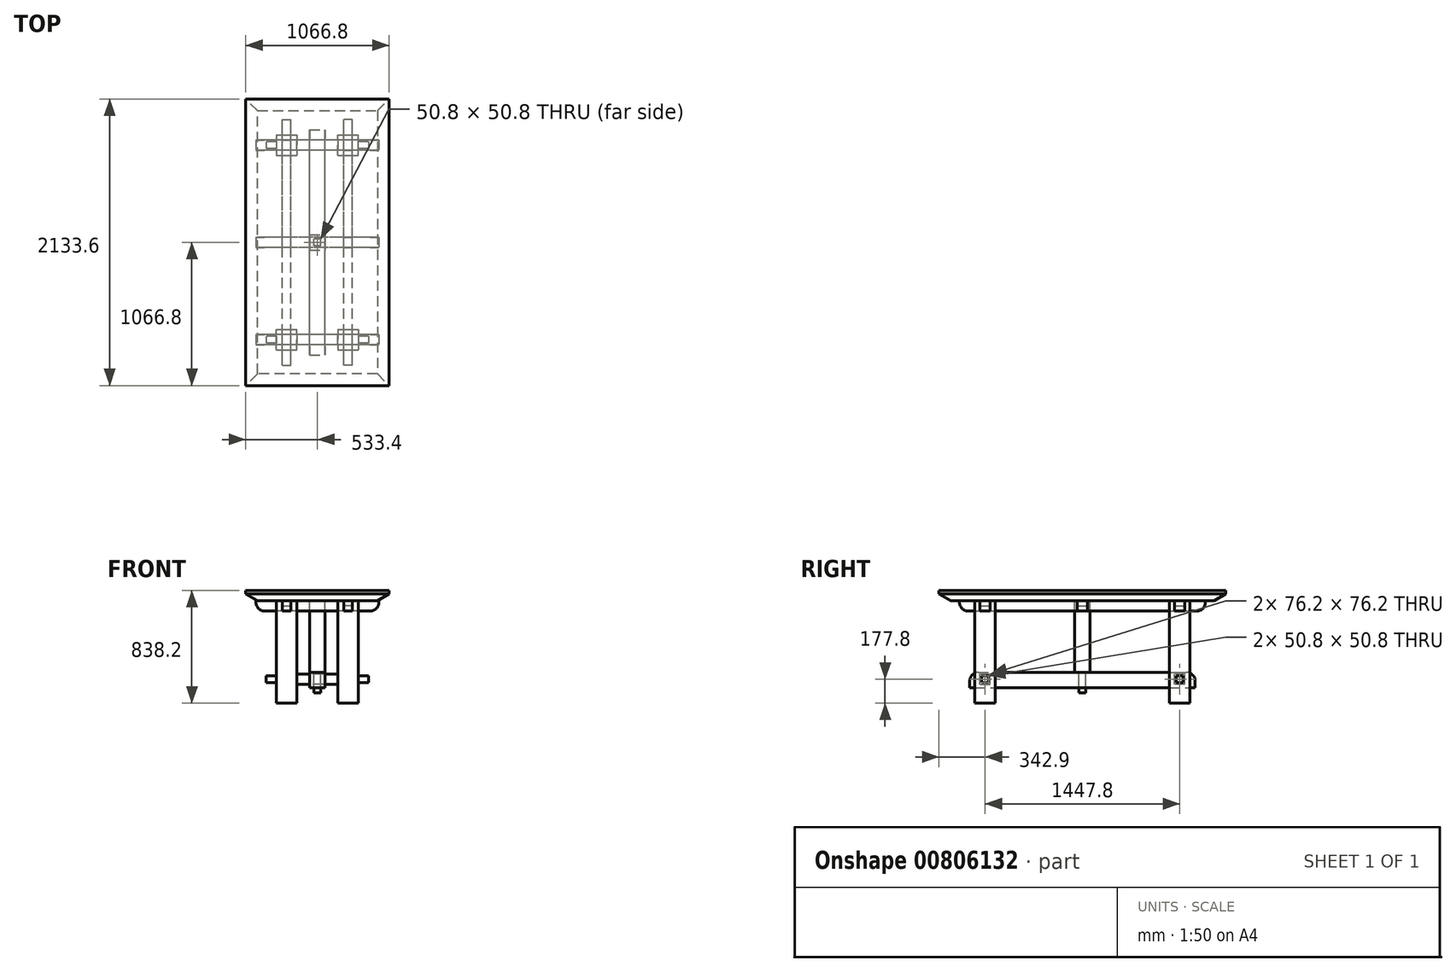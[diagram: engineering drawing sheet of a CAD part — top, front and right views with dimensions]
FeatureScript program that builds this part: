
annotation { "Feature Type Name" : "Feature", "Feature Type Description" : "" }
export const myFeature = defineFeature(function(context is Context, id is Id, definition is map)
    precondition{}
    {
        {
            var Q0;
            Q0=qCreatedBy(makeId("Top.planeOp"),FACE);
            var sketch = newSketch(context, id + "F0", { "sketchPlane" : qUnion([Q0])});
            skLineSegment(sketch, "E0.bottom", {"start": v(-533.4, -1066.8) * mm, "end": v(533.4, -1066.8) * mm});
            skLineSegment(sketch, "E0.top", {"start": v(-533.4, 1066.8) * mm, "end": v(533.4, 1066.8) * mm});
            skLineSegment(sketch, "E0.left", {"start": v(-533.4, -1066.8) * mm, "end": v(-533.4, 1066.8) * mm});
            skLineSegment(sketch, "E0.right", {"start": v(533.4, -1066.8) * mm, "end": v(533.4, 1066.8) * mm});
            skLineSegment(sketch, "E1", {"start": v(533.4, -1066.8) * mm, "end": v(-533.4, 1066.8) * mm, "construction": true});
            skSolve(sketch);
        }
        {
            var Q0;
            Q0 = qSketchRegion(id + "F0", true);
            extrude(context, id + "F1", {"entities" : qUnion([Q0]), "depth" : 76.2 * mm, "offsetDistance" : 25.4 * mm});
        }
        {
            var Q0;
            Q0=makeQuery(id+"F1.opExtrude","CAP_FACE",FACE,{"disambiguationData":[OSD([sQuery(id+"F0.wireOp",EDGE,"E0.bottom"),sQuery(id+"F0.wireOp",EDGE,"E0.top"),sQuery(id+"F0.wireOp",EDGE,"E0.left"),sQuery(id+"F0.wireOp",EDGE,"E0.right")])],"isStart":true});
            chamfer(context, id + "F2", {"entities" : qUnion([Q0]), "chamferType" : ChamferType.OFFSET_ANGLE, "width" : 50.8 * mm, "oppositeDirection" : false, "angle" : 60 * degree, "tangentPropagation" : true});
        }
        {
            var Q0;
            Q0=qCreatedBy(makeId("Right.planeOp"),FACE);
            var sketch = newSketch(context, id + "F3", { "sketchPlane" : qUnion([Q0])});
            skLineSegment(sketch, "E2.bottom", {"start": v(762, -76.2) * mm, "end": v(685.8, -76.2) * mm});
            skLineSegment(sketch, "E2.top", {"start": v(762, 0) * mm, "end": v(685.8, 0) * mm});
            skLineSegment(sketch, "E2.left", {"start": v(762, -76.2) * mm, "end": v(762, 0) * mm});
            skLineSegment(sketch, "E2.right", {"start": v(685.8, -76.2) * mm, "end": v(685.8, 0) * mm});
            skLineSegment(sketch, "E3.bottom", {"start": v(38.1, -76.2) * mm, "end": v(-38.1, -76.2) * mm});
            skLineSegment(sketch, "E3.top", {"start": v(38.1, 0) * mm, "end": v(-38.1, 0) * mm});
            skLineSegment(sketch, "E3.left", {"start": v(38.1, -76.2) * mm, "end": v(38.1, 0) * mm});
            skLineSegment(sketch, "E3.right", {"start": v(-38.1, -76.2) * mm, "end": v(-38.1, 0) * mm});
            skLineSegment(sketch, "E4.bottom", {"start": v(-685.8, -76.2) * mm, "end": v(-762, -76.2) * mm});
            skLineSegment(sketch, "E4.top", {"start": v(-685.8, 0) * mm, "end": v(-762, 0) * mm});
            skLineSegment(sketch, "E4.left", {"start": v(-685.8, -76.2) * mm, "end": v(-685.8, 0) * mm});
            skLineSegment(sketch, "E4.right", {"start": v(-762, -76.2) * mm, "end": v(-762, 0) * mm});
            skLineSegment(sketch, "E5", {"start": v(685.8, -76.2) * mm, "end": v(38.1, -76.2) * mm, "construction": true});
            skLineSegment(sketch, "E6", {"start": v(-38.1, -76.2) * mm, "end": v(-685.8, -76.2) * mm, "construction": true});
            skSolve(sketch);
        }
        {
            var Q0;
            Q0 = qSketchRegion(id + "F3", true);
            extrude(context, id + "F4", {"entities" : qUnion([Q0]), "endBound" : BoundingType.SYMMETRIC, "depth" : 914.4 * mm, "offsetDistance" : 25.4 * mm});
        }
        {
            var Q0;
            Q0=makeQuery(id+"F4.opExtrude","SWEPT_FACE",FACE,{"disambiguationData":[OSD([sQuery(id+"F3.wireOp",EDGE,"E2.left")])]});
            var sketch = newSketch(context, id + "F5", { "sketchPlane" : qUnion([Q0])});
            skLineSegment(sketch, "E7.bottom", {"start": v(-260.35, 0) * mm, "end": v(-196.85, 0) * mm});
            skLineSegment(sketch, "E7.top", {"start": v(-260.35, -38.1) * mm, "end": v(-196.85, -38.1) * mm});
            skLineSegment(sketch, "E7.left", {"start": v(-260.35, 0) * mm, "end": v(-260.35, -38.1) * mm});
            skLineSegment(sketch, "E7.right", {"start": v(-196.85, 0) * mm, "end": v(-196.85, -38.1) * mm});
            skLineSegment(sketch, "E8.bottom", {"start": v(260.35, 0) * mm, "end": v(196.85, 0) * mm});
            skLineSegment(sketch, "E8.top", {"start": v(260.35, -38.1) * mm, "end": v(196.85, -38.1) * mm});
            skLineSegment(sketch, "E8.left", {"start": v(196.85, 0) * mm, "end": v(196.85, -38.1) * mm});
            skLineSegment(sketch, "E8.right", {"start": v(260.35, 0) * mm, "end": v(260.35, -38.1) * mm});
            skLineSegment(sketch, "E9", {"start": v(-228.6, -38.1) * mm, "end": v(-228.6, -76.2) * mm, "construction": true});
            skLineSegment(sketch, "E10", {"start": v(228.6, -38.1) * mm, "end": v(228.6, -76.2) * mm, "construction": true});
            skLineSegment(sketch, "E11", {"start": v(-457.2, -38.1) * mm, "end": v(-260.35, -38.1) * mm, "construction": true});
            skLineSegment(sketch, "E12", {"start": v(260.35, -38.1) * mm, "end": v(457.2, -38.1) * mm, "construction": true});
            skSolve(sketch);
        }
        {
            var Q0;
            Q0 = qSketchRegion(id + "F5", true);
            extrude(context, id + "F6", {"entities" : qUnion([Q0]), "operationType" : NewBodyOperationType.REMOVE, "endBound" : BoundingType.THROUGH_ALL, "oppositeDirection" : true, "depth" : 25.4 * mm, "offsetDistance" : 25.4 * mm});
        }
        {
            var Q0;
            Q0=qCreatedBy(makeId("Front.planeOp"),FACE);
            var sketch = newSketch(context, id + "F7", { "sketchPlane" : qUnion([Q0])});
            skLineSegment(sketch, "E13.bottom", {"start": v(260.35, 0) * mm, "end": v(196.85, 0) * mm});
            skLineSegment(sketch, "E13.top", {"start": v(260.35, -76.2) * mm, "end": v(196.85, -76.2) * mm});
            skLineSegment(sketch, "E13.left", {"start": v(260.35, 0) * mm, "end": v(260.35, -76.2) * mm});
            skLineSegment(sketch, "E13.right", {"start": v(196.85, 0) * mm, "end": v(196.85, -76.2) * mm});
            skLineSegment(sketch, "E14.bottom", {"start": v(-260.35, 0) * mm, "end": v(-196.85, 0) * mm});
            skLineSegment(sketch, "E14.top", {"start": v(-260.35, -76.2) * mm, "end": v(-196.85, -76.2) * mm});
            skLineSegment(sketch, "E14.left", {"start": v(-260.35, 0) * mm, "end": v(-260.35, -76.2) * mm});
            skLineSegment(sketch, "E14.right", {"start": v(-196.85, 0) * mm, "end": v(-196.85, -76.2) * mm});
            skSolve(sketch);
        }
        {
            var Q0;
            Q0 = qSketchRegion(id + "F7", true);
            extrude(context, id + "F8", {"entities" : qUnion([Q0]), "endBound" : BoundingType.SYMMETRIC, "depth" : 1828.8 * mm, "offsetDistance" : 25.4 * mm});
        }
        {
            var Q0;
            Q0=makeQuery(id+"F4.opExtrude","SWEPT_BODY",BODY,{"disambiguationData":[OSD([sQuery(id+"F3.wireOp",EDGE,"E2.bottom"),sQuery(id+"F3.wireOp",EDGE,"E2.top"),sQuery(id+"F3.wireOp",EDGE,"E2.left"),sQuery(id+"F3.wireOp",EDGE,"E2.right")])]});
            var Q1;
            Q1=makeQuery(id+"F4.opExtrude","SWEPT_BODY",BODY,{"disambiguationData":[OSD([sQuery(id+"F3.wireOp",EDGE,"E3.bottom"),sQuery(id+"F3.wireOp",EDGE,"E3.top"),sQuery(id+"F3.wireOp",EDGE,"E3.left"),sQuery(id+"F3.wireOp",EDGE,"E3.right")])]});
            var Q2;
            Q2=makeQuery(id+"F4.opExtrude","SWEPT_BODY",BODY,{"disambiguationData":[OSD([sQuery(id+"F3.wireOp",EDGE,"E4.bottom"),sQuery(id+"F3.wireOp",EDGE,"E4.top"),sQuery(id+"F3.wireOp",EDGE,"E4.left"),sQuery(id+"F3.wireOp",EDGE,"E4.right")])]});
            var Q3;
            Q3=makeQuery(id+"F8.opExtrude","SWEPT_BODY",BODY,{"disambiguationData":[OSD([sQuery(id+"F7.wireOp",EDGE,"E13.bottom"),sQuery(id+"F7.wireOp",EDGE,"E13.top"),sQuery(id+"F7.wireOp",EDGE,"E13.left"),sQuery(id+"F7.wireOp",EDGE,"E13.right")])]});
            var Q4;
            Q4=makeQuery(id+"F8.opExtrude","SWEPT_BODY",BODY,{"disambiguationData":[OSD([sQuery(id+"F7.wireOp",EDGE,"E14.bottom"),sQuery(id+"F7.wireOp",EDGE,"E14.top"),sQuery(id+"F7.wireOp",EDGE,"E14.left"),sQuery(id+"F7.wireOp",EDGE,"E14.right")])]});
            booleanBodies(context, id + "F9", {"operationType" : BooleanOperationType.SUBTRACTION, "tools" : qUnion([Q0, Q1, Q2]), "targets" : qUnion([Q3, Q4]), "keepTools" : true});
        }
        {
            var Q0;
            Q0=makeQuery(id+"F1.opExtrude","CAP_FACE",FACE,{"disambiguationData":[OSD([sQuery(id+"F0.wireOp",EDGE,"E0.bottom"),sQuery(id+"F0.wireOp",EDGE,"E0.top"),sQuery(id+"F0.wireOp",EDGE,"E0.left"),sQuery(id+"F0.wireOp",EDGE,"E0.right")])],"isStart":true});
            var sketch = newSketch(context, id + "F10", { "sketchPlane" : qUnion([Q0])});
            skLineSegment(sketch, "E15.bottom", {"start": v(-57.15, -57.15) * mm, "end": v(57.15, -57.15) * mm});
            skLineSegment(sketch, "E15.top", {"start": v(-57.15, 57.15) * mm, "end": v(57.15, 57.15) * mm});
            skLineSegment(sketch, "E15.left", {"start": v(-57.15, -57.15) * mm, "end": v(-57.15, 57.15) * mm});
            skLineSegment(sketch, "E15.right", {"start": v(57.15, -57.15) * mm, "end": v(57.15, 57.15) * mm});
            skLineSegment(sketch, "E16", {"start": v(-57.15, 57.15) * mm, "end": v(57.15, -57.15) * mm, "construction": true});
            skSolve(sketch);
        }
        {
            var Q0;
            Q0 = qSketchRegion(id + "F10", true);
            extrude(context, id + "F11", {"entities" : qUnion([Q0]), "depth" : 533.4 * mm, "offsetDistance" : 25.4 * mm});
        }
        {
            var Q0;
            Q0=makeQuery(id+"F4.opExtrude","SWEPT_BODY",BODY,{"disambiguationData":[OSD([sQuery(id+"F3.wireOp",EDGE,"E3.bottom"),sQuery(id+"F3.wireOp",EDGE,"E3.top"),sQuery(id+"F3.wireOp",EDGE,"E3.left"),sQuery(id+"F3.wireOp",EDGE,"E3.right")])]});
            var Q1;
            Q1=makeQuery(id+"F11.opExtrude","SWEPT_BODY",BODY,{"disambiguationData":[OSD([sQuery(id+"F10.wireOp",EDGE,"E15.bottom"),sQuery(id+"F10.wireOp",EDGE,"E15.top"),sQuery(id+"F10.wireOp",EDGE,"E15.left"),sQuery(id+"F10.wireOp",EDGE,"E15.right")])]});
            booleanBodies(context, id + "F12", {"operationType" : BooleanOperationType.SUBTRACTION, "tools" : qUnion([Q0]), "targets" : qUnion([Q1]), "keepTools" : true});
        }
        {
            var Q0;
            Q0=makeQuery(id+"F1.opExtrude","CAP_FACE",FACE,{"disambiguationData":[OSD([sQuery(id+"F0.wireOp",EDGE,"E0.bottom"),sQuery(id+"F0.wireOp",EDGE,"E0.top"),sQuery(id+"F0.wireOp",EDGE,"E0.left"),sQuery(id+"F0.wireOp",EDGE,"E0.right")])],"isStart":true});
            var sketch = newSketch(context, id + "F13", { "sketchPlane" : qUnion([Q0])});
            skLineSegment(sketch, "E17.bottom", {"start": v(152.4, 647.7) * mm, "end": v(304.8, 647.7) * mm});
            skLineSegment(sketch, "E17.top", {"start": v(152.4, 800.1) * mm, "end": v(304.8, 800.1) * mm});
            skLineSegment(sketch, "E17.left", {"start": v(152.4, 647.7) * mm, "end": v(152.4, 800.1) * mm});
            skLineSegment(sketch, "E17.right", {"start": v(304.8, 647.7) * mm, "end": v(304.8, 800.1) * mm});
            skLineSegment(sketch, "E18.bottom", {"start": v(152.4, -647.7) * mm, "end": v(304.8, -647.7) * mm});
            skLineSegment(sketch, "E18.top", {"start": v(152.4, -800.1) * mm, "end": v(304.8, -800.1) * mm});
            skLineSegment(sketch, "E18.left", {"start": v(152.4, -647.7) * mm, "end": v(152.4, -800.1) * mm});
            skLineSegment(sketch, "E18.right", {"start": v(304.8, -647.7) * mm, "end": v(304.8, -800.1) * mm});
            skLineSegment(sketch, "E19.bottom", {"start": v(-304.8, -800.1) * mm, "end": v(-152.4, -800.1) * mm});
            skLineSegment(sketch, "E19.top", {"start": v(-304.8, -647.7) * mm, "end": v(-152.4, -647.7) * mm});
            skLineSegment(sketch, "E19.left", {"start": v(-304.8, -800.1) * mm, "end": v(-304.8, -647.7) * mm});
            skLineSegment(sketch, "E19.right", {"start": v(-152.4, -800.1) * mm, "end": v(-152.4, -647.7) * mm});
            skLineSegment(sketch, "E20.bottom", {"start": v(-304.8, 800.1) * mm, "end": v(-152.4, 800.1) * mm});
            skLineSegment(sketch, "E20.top", {"start": v(-304.8, 647.7) * mm, "end": v(-152.4, 647.7) * mm});
            skLineSegment(sketch, "E20.left", {"start": v(-304.8, 800.1) * mm, "end": v(-304.8, 647.7) * mm});
            skLineSegment(sketch, "E20.right", {"start": v(-152.4, 800.1) * mm, "end": v(-152.4, 647.7) * mm});
            skLineSegment(sketch, "E21", {"start": v(-144.46, 565.34) * mm, "end": v(-140.26, 569.66) * mm, "construction": true});
            skLineSegment(sketch, "E22", {"start": v(-152.4, 647.7) * mm, "end": v(-304.8, 800.1) * mm, "construction": true});
            skLineSegment(sketch, "E23", {"start": v(-196.85, 762) * mm, "end": v(-228.6, 723.9) * mm, "construction": true});
            skLineSegment(sketch, "E24", {"start": v(-228.6, 723.9) * mm, "end": v(-260.35, 685.8) * mm, "construction": true});
            skLineSegment(sketch, "E25", {"start": v(260.35, -685.8) * mm, "end": v(228.6, -723.9) * mm, "construction": true});
            skLineSegment(sketch, "E26", {"start": v(228.6, -723.9) * mm, "end": v(196.85, -762) * mm, "construction": true});
            skLineSegment(sketch, "E27", {"start": v(152.4, -647.7) * mm, "end": v(304.8, -800.1) * mm, "construction": true});
            skSolve(sketch);
        }
        {
            var Q0;
            Q0 = qSketchRegion(id + "F13", true);
            extrude(context, id + "F14", {"entities" : qUnion([Q0]), "depth" : 762 * mm, "offsetDistance" : 25.4 * mm});
        }
        {
            var Q0;
            Q0=makeQuery(id+"F4.opExtrude","SWEPT_BODY",BODY,{"disambiguationData":[OSD([sQuery(id+"F3.wireOp",EDGE,"E4.bottom"),sQuery(id+"F3.wireOp",EDGE,"E4.top"),sQuery(id+"F3.wireOp",EDGE,"E4.left"),sQuery(id+"F3.wireOp",EDGE,"E4.right")])]});
            var Q1;
            Q1=makeQuery(id+"F8.opExtrude","SWEPT_BODY",BODY,{"disambiguationData":[OSD([sQuery(id+"F7.wireOp",EDGE,"E14.bottom"),sQuery(id+"F7.wireOp",EDGE,"E14.top"),sQuery(id+"F7.wireOp",EDGE,"E14.left"),sQuery(id+"F7.wireOp",EDGE,"E14.right")])]});
            var Q2;
            Q2=makeQuery(id+"F8.opExtrude","SWEPT_BODY",BODY,{"disambiguationData":[OSD([sQuery(id+"F7.wireOp",EDGE,"E13.bottom"),sQuery(id+"F7.wireOp",EDGE,"E13.top"),sQuery(id+"F7.wireOp",EDGE,"E13.left"),sQuery(id+"F7.wireOp",EDGE,"E13.right")])]});
            var Q3;
            Q3=makeQuery(id+"F4.opExtrude","SWEPT_BODY",BODY,{"disambiguationData":[OSD([sQuery(id+"F3.wireOp",EDGE,"E3.bottom"),sQuery(id+"F3.wireOp",EDGE,"E3.top"),sQuery(id+"F3.wireOp",EDGE,"E3.left"),sQuery(id+"F3.wireOp",EDGE,"E3.right")])]});
            var Q4;
            Q4=makeQuery(id+"F4.opExtrude","SWEPT_BODY",BODY,{"disambiguationData":[OSD([sQuery(id+"F3.wireOp",EDGE,"E2.bottom"),sQuery(id+"F3.wireOp",EDGE,"E2.top"),sQuery(id+"F3.wireOp",EDGE,"E2.left"),sQuery(id+"F3.wireOp",EDGE,"E2.right")])]});
            var Q5;
            Q5=makeQuery(id+"F14.opExtrude","SWEPT_BODY",BODY,{"disambiguationData":[OSD([sQuery(id+"F13.wireOp",EDGE,"E17.bottom"),sQuery(id+"F13.wireOp",EDGE,"E17.top"),sQuery(id+"F13.wireOp",EDGE,"E17.left"),sQuery(id+"F13.wireOp",EDGE,"E17.right")])]});
            var Q6;
            Q6=makeQuery(id+"F14.opExtrude","SWEPT_BODY",BODY,{"disambiguationData":[OSD([sQuery(id+"F13.wireOp",EDGE,"E20.bottom"),sQuery(id+"F13.wireOp",EDGE,"E20.top"),sQuery(id+"F13.wireOp",EDGE,"E20.left"),sQuery(id+"F13.wireOp",EDGE,"E20.right")])]});
            var Q7;
            Q7=makeQuery(id+"F14.opExtrude","SWEPT_BODY",BODY,{"disambiguationData":[OSD([sQuery(id+"F13.wireOp",EDGE,"E19.bottom"),sQuery(id+"F13.wireOp",EDGE,"E19.top"),sQuery(id+"F13.wireOp",EDGE,"E19.left"),sQuery(id+"F13.wireOp",EDGE,"E19.right")])]});
            var Q8;
            Q8=makeQuery(id+"F14.opExtrude","SWEPT_BODY",BODY,{"disambiguationData":[OSD([sQuery(id+"F13.wireOp",EDGE,"E18.bottom"),sQuery(id+"F13.wireOp",EDGE,"E18.top"),sQuery(id+"F13.wireOp",EDGE,"E18.left"),sQuery(id+"F13.wireOp",EDGE,"E18.right")])]});
            booleanBodies(context, id + "F15", {"operationType" : BooleanOperationType.SUBTRACTION, "tools" : qUnion([Q0, Q1, Q2, Q3, Q4]), "targets" : qUnion([Q5, Q6, Q7, Q8]), "keepTools" : true});
        }
        {
            var Q0;
            Q0=makeQuery(id+"F11.opExtrude","CAP_FACE",FACE,{"disambiguationData":[OSD([sQuery(id+"F10.wireOp",EDGE,"E15.bottom"),sQuery(id+"F10.wireOp",EDGE,"E15.top"),sQuery(id+"F10.wireOp",EDGE,"E15.left"),sQuery(id+"F10.wireOp",EDGE,"E15.right")])],"isStart":false});
            var sketch = newSketch(context, id + "F16", { "sketchPlane" : qUnion([Q0])});
            skLineSegment(sketch, "E28.bottom", {"start": v(25.4, 25.4) * mm, "end": v(-25.4, 25.4) * mm});
            skLineSegment(sketch, "E28.top", {"start": v(25.4, -25.4) * mm, "end": v(-25.4, -25.4) * mm});
            skLineSegment(sketch, "E28.left", {"start": v(25.4, 25.4) * mm, "end": v(25.4, -25.4) * mm});
            skLineSegment(sketch, "E28.right", {"start": v(-25.4, 25.4) * mm, "end": v(-25.4, -25.4) * mm});
            skLineSegment(sketch, "E29", {"start": v(0, -57.15) * mm, "end": v(0, -25.4) * mm, "construction": true});
            skLineSegment(sketch, "E30", {"start": v(-25.4, 0) * mm, "end": v(-57.15, 0) * mm, "construction": true});
            skLineSegment(sketch, "E31", {"start": v(0, 25.4) * mm, "end": v(0, 57.15) * mm, "construction": true});
            skLineSegment(sketch, "E32", {"start": v(25.4, 0) * mm, "end": v(57.15, 0) * mm, "construction": true});
            skSolve(sketch);
        }
        {
            var Q0;
            Q0 = qSketchRegion(id + "F16", true);
            extrude(context, id + "F17", {"entities" : qUnion([Q0]), "operationType" : NewBodyOperationType.ADD, "depth" : 152.4 * mm, "offsetDistance" : 25.4 * mm});
        }
        {
            var Q0;
            Q0=makeQuery(id+"F14.opExtrude","SWEPT_FACE",FACE,{"disambiguationData":[OSD([sQuery(id+"F13.wireOp",EDGE,"E19.left")])]});
            var sketch = newSketch(context, id + "F18", { "sketchPlane" : qUnion([Q0])});
            skLineSegment(sketch, "E33.bottom", {"start": v(-749.3, -609.6) * mm, "end": v(-698.5, -609.6) * mm});
            skLineSegment(sketch, "E33.top", {"start": v(-749.3, -558.8) * mm, "end": v(-698.5, -558.8) * mm});
            skLineSegment(sketch, "E33.left", {"start": v(-749.3, -609.6) * mm, "end": v(-749.3, -558.8) * mm});
            skLineSegment(sketch, "E33.right", {"start": v(-698.5, -609.6) * mm, "end": v(-698.5, -558.8) * mm});
            skLineSegment(sketch, "E34.bottom", {"start": v(698.5, -609.6) * mm, "end": v(749.3, -609.6) * mm});
            skLineSegment(sketch, "E34.top", {"start": v(698.5, -558.8) * mm, "end": v(749.3, -558.8) * mm});
            skLineSegment(sketch, "E34.left", {"start": v(698.5, -609.6) * mm, "end": v(698.5, -558.8) * mm});
            skLineSegment(sketch, "E34.right", {"start": v(749.3, -609.6) * mm, "end": v(749.3, -558.8) * mm});
            skLineSegment(sketch, "E35", {"start": v(749.3, -584.2) * mm, "end": v(800.1, -584.2) * mm, "construction": true});
            skLineSegment(sketch, "E36", {"start": v(698.5, -584.2) * mm, "end": v(647.7, -584.2) * mm, "construction": true});
            skLineSegment(sketch, "E37", {"start": v(-698.5, -584.2) * mm, "end": v(-647.7, -584.2) * mm, "construction": true});
            skPoint(sketch, "E37.endSnap0", {"position": v(-698.5, -584.2) * mm});
            skLineSegment(sketch, "E38", {"start": v(-749.3, -584.2) * mm, "end": v(-800.1, -584.2) * mm, "construction": true});
            skSolve(sketch);
        }
        {
            var Q0;
            Q0 = qSketchRegion(id + "F18", true);
            extrude(context, id + "F19", {"entities" : qUnion([Q0]), "operationType" : NewBodyOperationType.REMOVE, "endBound" : BoundingType.THROUGH_ALL, "oppositeDirection" : true, "depth" : 25.4 * mm, "offsetDistance" : 25.4 * mm});
        }
        {
            var Q0;
            Q0=qCreatedBy(makeId("Right.planeOp"),FACE);
            var sketch = newSketch(context, id + "F20", { "sketchPlane" : qUnion([Q0])});
            skLineSegment(sketch, "E39.bottom", {"start": v(749.3, -609.6) * mm, "end": v(698.5, -609.6) * mm});
            skLineSegment(sketch, "E39.top", {"start": v(749.3, -558.8) * mm, "end": v(698.5, -558.8) * mm});
            skLineSegment(sketch, "E39.left", {"start": v(749.3, -609.6) * mm, "end": v(749.3, -558.8) * mm});
            skLineSegment(sketch, "E39.right", {"start": v(698.5, -609.6) * mm, "end": v(698.5, -558.8) * mm});
            skLineSegment(sketch, "E40.bottom", {"start": v(-698.5, -609.6) * mm, "end": v(-749.3, -609.6) * mm});
            skLineSegment(sketch, "E40.top", {"start": v(-698.5, -558.8) * mm, "end": v(-749.3, -558.8) * mm});
            skLineSegment(sketch, "E40.left", {"start": v(-698.5, -609.6) * mm, "end": v(-698.5, -558.8) * mm});
            skLineSegment(sketch, "E40.right", {"start": v(-749.3, -609.6) * mm, "end": v(-749.3, -558.8) * mm});
            skSolve(sketch);
        }
        {
            var Q0;
            Q0 = qSketchRegion(id + "F20", true);
            extrude(context, id + "F21", {"entities" : qUnion([Q0]), "endBound" : BoundingType.SYMMETRIC, "depth" : 762 * mm, "offsetDistance" : 25.4 * mm});
        }
        {
            var Q0;
            Q0=qCreatedBy(makeId("Right.planeOp"),FACE);
            var sketch = newSketch(context, id + "F22", { "sketchPlane" : qUnion([Q0])});
            skLineSegment(sketch, "E41.bottom", {"start": v(-685.8, -546.1) * mm, "end": v(-762, -546.1) * mm});
            skLineSegment(sketch, "E41.top", {"start": v(-685.8, -622.3) * mm, "end": v(-762, -622.3) * mm});
            skLineSegment(sketch, "E41.left", {"start": v(-685.8, -546.1) * mm, "end": v(-685.8, -622.3) * mm});
            skLineSegment(sketch, "E41.right", {"start": v(-762, -546.1) * mm, "end": v(-762, -622.3) * mm});
            skLineSegment(sketch, "E42.bottom", {"start": v(685.8, -546.1) * mm, "end": v(762, -546.1) * mm});
            skLineSegment(sketch, "E42.top", {"start": v(685.8, -622.3) * mm, "end": v(762, -622.3) * mm});
            skLineSegment(sketch, "E42.left", {"start": v(685.8, -546.1) * mm, "end": v(685.8, -622.3) * mm});
            skLineSegment(sketch, "E42.right", {"start": v(762, -546.1) * mm, "end": v(762, -622.3) * mm});
            skLineSegment(sketch, "E43", {"start": v(723.9, -546.1) * mm, "end": v(723.9, -558.8) * mm, "construction": true});
            skLineSegment(sketch, "E44", {"start": v(685.8, -584.2) * mm, "end": v(698.5, -584.2) * mm, "construction": true});
            skLineSegment(sketch, "E45", {"start": v(723.9, -622.3) * mm, "end": v(723.9, -609.6) * mm, "construction": true});
            skPoint(sketch, "E45.endSnap0", {"position": v(723.9, -622.3) * mm});
            skLineSegment(sketch, "E46", {"start": v(762, -584.2) * mm, "end": v(749.3, -584.2) * mm, "construction": true});
            skLineSegment(sketch, "E47", {"start": v(-723.9, -546.1) * mm, "end": v(-723.9, -558.8) * mm, "construction": true});
            skLineSegment(sketch, "E48", {"start": v(-723.9, -622.3) * mm, "end": v(-723.9, -609.6) * mm, "construction": true});
            skLineSegment(sketch, "E49", {"start": v(-762, -584.2) * mm, "end": v(-749.3, -584.2) * mm, "construction": true});
            skLineSegment(sketch, "E50", {"start": v(-685.8, -584.2) * mm, "end": v(-698.5, -584.2) * mm, "construction": true});
            skSolve(sketch);
        }
        {
            var Q0;
            Q0 = qSketchRegion(id + "F22", true);
            var Q1;
            Q1=makeQuery(id+"F14.opExtrude","SWEPT_FACE",FACE,{"disambiguationData":[OSD([sQuery(id+"F13.wireOp",EDGE,"E17.left")])]});
            var Q2;
            Q2=makeQuery(id+"F14.opExtrude","SWEPT_FACE",FACE,{"disambiguationData":[OSD([sQuery(id+"F13.wireOp",EDGE,"E20.right")])]});
            extrude(context, id + "F23", {"entities" : qUnion([Q0]), "operationType" : NewBodyOperationType.ADD, "endBound" : BoundingType.UP_TO_SURFACE, "depth" : 25.4 * mm, "endBoundEntityFace" : qUnion([Q1]), "offsetDistance" : 25.4 * mm, "hasSecondDirection" : true, "secondDirectionBound" : SecondDirectionBoundingType.UP_TO_SURFACE, "secondDirectionOppositeDirection" : true, "secondDirectionDepth" : 25.4 * mm, "secondDirectionBoundEntityFace" : qUnion([Q2])});
        }
        {
            var Q0;
            Q0=qCreatedBy(makeId("Front.planeOp"),FACE);
            var sketch = newSketch(context, id + "F24", { "sketchPlane" : qUnion([Q0])});
            skLineSegment(sketch, "E51.bottom", {"start": v(-57.15, -533.4) * mm, "end": v(57.15, -533.4) * mm});
            skLineSegment(sketch, "E51.top", {"start": v(-57.15, -647.7) * mm, "end": v(57.15, -647.7) * mm});
            skLineSegment(sketch, "E51.left", {"start": v(-57.15, -533.4) * mm, "end": v(-57.15, -647.7) * mm});
            skLineSegment(sketch, "E51.right", {"start": v(57.15, -533.4) * mm, "end": v(57.15, -647.7) * mm});
            skSolve(sketch);
        }
        {
            var Q0;
            Q0 = qSketchRegion(id + "F24", true);
            extrude(context, id + "F25", {"entities" : qUnion([Q0]), "endBound" : BoundingType.SYMMETRIC, "depth" : 1676.4 * mm, "offsetDistance" : 25.4 * mm});
        }
        {
            var Q0;
            Q0=makeQuery(id+"F21.opExtrude","SWEPT_BODY",BODY,{"disambiguationData":[OSD([sQuery(id+"F20.wireOp",EDGE,"E39.bottom"),sQuery(id+"F20.wireOp",EDGE,"E39.top"),sQuery(id+"F20.wireOp",EDGE,"E39.left"),sQuery(id+"F20.wireOp",EDGE,"E39.right")])]});
            var Q1;
            Q1=makeQuery(id+"F11.opExtrude","SWEPT_BODY",BODY,{"disambiguationData":[OSD([sQuery(id+"F10.wireOp",EDGE,"E15.bottom"),sQuery(id+"F10.wireOp",EDGE,"E15.top"),sQuery(id+"F10.wireOp",EDGE,"E15.left"),sQuery(id+"F10.wireOp",EDGE,"E15.right")])]});
            var Q2;
            Q2=makeQuery(id+"F21.opExtrude","SWEPT_BODY",BODY,{"disambiguationData":[OSD([sQuery(id+"F20.wireOp",EDGE,"E40.bottom"),sQuery(id+"F20.wireOp",EDGE,"E40.top"),sQuery(id+"F20.wireOp",EDGE,"E40.left"),sQuery(id+"F20.wireOp",EDGE,"E40.right")])]});
            var Q3;
            Q3=makeQuery(id+"F25.opExtrude","SWEPT_BODY",BODY,{"disambiguationData":[OSD([sQuery(id+"F24.wireOp",EDGE,"E51.bottom"),sQuery(id+"F24.wireOp",EDGE,"E51.top"),sQuery(id+"F24.wireOp",EDGE,"E51.left"),sQuery(id+"F24.wireOp",EDGE,"E51.right")])]});
            booleanBodies(context, id + "F26", {"operationType" : BooleanOperationType.SUBTRACTION, "tools" : qUnion([Q0, Q1, Q2]), "targets" : qUnion([Q3]), "keepTools" : true});
        }
        {
            var Q0;
            Q0=makeQuery(id+"F4.opExtrude","CAP_EDGE",EDGE,{"disambiguationData":[OSD([sQuery(id+"F3.wireOp",EDGE,"E2.bottom")])],"isStart":true});
            var Q1;
            Q1=makeQuery(id+"F4.opExtrude","CAP_EDGE",EDGE,{"disambiguationData":[OSD([sQuery(id+"F3.wireOp",EDGE,"E3.bottom")])],"isStart":true});
            var Q2;
            Q2=makeQuery(id+"F4.opExtrude","CAP_EDGE",EDGE,{"disambiguationData":[OSD([sQuery(id+"F3.wireOp",EDGE,"E4.bottom")])],"isStart":true});
            var Q3;
            Q3=makeQuery(id+"F8.opExtrude","CAP_EDGE",EDGE,{"disambiguationData":[OSD([sQuery(id+"F7.wireOp",EDGE,"E14.top")])],"isStart":false});
            var Q4;
            Q4=makeQuery(id+"F8.opExtrude","CAP_EDGE",EDGE,{"disambiguationData":[OSD([sQuery(id+"F7.wireOp",EDGE,"E13.top")])],"isStart":false});
            var Q5;
            Q5=makeQuery(id+"F25.opExtrude","CAP_EDGE",EDGE,{"disambiguationData":[OSD([sQuery(id+"F24.wireOp",EDGE,"E51.bottom")])],"isStart":false});
            var Q6;
            Q6=makeQuery(id+"F4.opExtrude","CAP_EDGE",EDGE,{"disambiguationData":[OSD([sQuery(id+"F3.wireOp",EDGE,"E4.bottom")])],"isStart":false});
            var Q7;
            Q7=makeQuery(id+"F4.opExtrude","CAP_EDGE",EDGE,{"disambiguationData":[OSD([sQuery(id+"F3.wireOp",EDGE,"E3.bottom")])],"isStart":false});
            var Q8;
            Q8=makeQuery(id+"F4.opExtrude","CAP_EDGE",EDGE,{"disambiguationData":[OSD([sQuery(id+"F3.wireOp",EDGE,"E2.bottom")])],"isStart":false});
            var Q9;
            Q9=makeQuery(id+"F8.opExtrude","CAP_EDGE",EDGE,{"disambiguationData":[OSD([sQuery(id+"F7.wireOp",EDGE,"E13.top")])],"isStart":true});
            var Q10;
            Q10=makeQuery(id+"F8.opExtrude","CAP_EDGE",EDGE,{"disambiguationData":[OSD([sQuery(id+"F7.wireOp",EDGE,"E14.top")])],"isStart":true});
            var Q11;
            Q11=makeQuery(id+"F25.opExtrude","CAP_EDGE",EDGE,{"disambiguationData":[OSD([sQuery(id+"F24.wireOp",EDGE,"E51.bottom")])],"isStart":true});
            fillet(context, id + "F27", {"entities" : qUnion([Q0, Q1, Q2, Q3, Q4, Q5, Q6, Q7, Q8, Q9, Q10, Q11]), "radius" : 63.5 * mm, "tangentPropagation" : true, "allowEdgeOverflow" : false});
        }
    });
